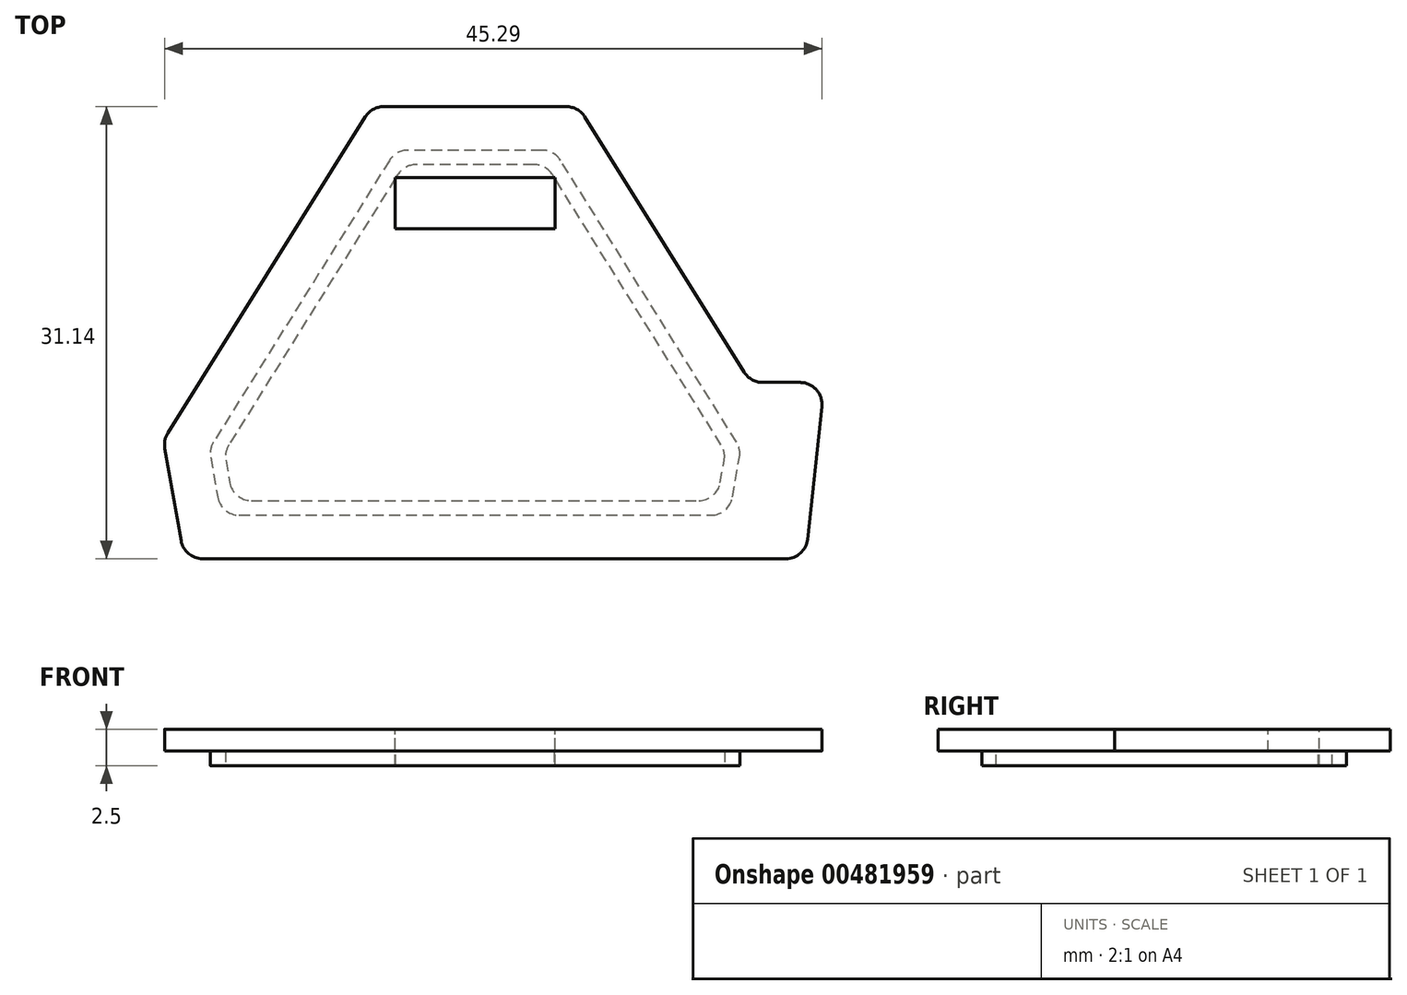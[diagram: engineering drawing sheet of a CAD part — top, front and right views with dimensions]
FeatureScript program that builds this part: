
annotation { "Feature Type Name" : "Feature", "Feature Type Description" : "" }
export const myFeature = defineFeature(function(context is Context, id is Id, definition is map)
    precondition{}
    {
        {
            var Q0;
            Q0=qCreatedBy(makeId("Top.planeOp"),FACE);
            var sketch = newSketch(context, id + "F0", { "sketchPlane" : qUnion([Q0])});
            skLineSegment(sketch, "E0.0", {"start": v(-7.77, 38.07) * mm, "end": v(6.47, 38.07) * mm});
            skLineSegment(sketch, "E1.0", {"start": v(6.47, 38.07) * mm, "end": v(20.82, 15.1) * mm});
            skLineSegment(sketch, "E2.0", {"start": v(19.38, 6.93) * mm, "end": v(20.82, 15.1) * mm});
            skLineSegment(sketch, "E3.0", {"start": v(-20.68, 6.93) * mm, "end": v(19.38, 6.93) * mm});
            skLineSegment(sketch, "E4.0", {"start": v(-20.68, 6.93) * mm, "end": v(-22.12, 15.1) * mm});
            skLineSegment(sketch, "E5.0", {"start": v(-22.12, 15.1) * mm, "end": v(-7.77, 38.07) * mm});
            skSolve(sketch);
        }
        {
            var Q0;
            Q0 = qSketchRegion(id + "F0", true);
            extrude(context, id + "F1", {"entities" : qUnion([Q0]), "depth" : 1.5 * mm});
        }
        {
            var Q0;
            Q0=makeQuery(id+"F1.opExtrude","CAP_FACE",FACE,{"disambiguationData":[OSD([sQuery(id+"F0.wireOp",EDGE,"E0.0"),sQuery(id+"F0.wireOp",EDGE,"E1.0"),sQuery(id+"F0.wireOp",EDGE,"E2.0"),sQuery(id+"F0.wireOp",EDGE,"E3.0"),sQuery(id+"F0.wireOp",EDGE,"E4.0"),sQuery(id+"F0.wireOp",EDGE,"E5.0")])],"isStart":true});
            var sketch = newSketch(context, id + "F2", { "sketchPlane" : qUnion([Q0])});
            skLineSegment(sketch, "E6.0", {"start": v(-18.97, -14.48) * mm, "end": v(-18.16, -9.93) * mm});
            skLineSegment(sketch, "E6.1", {"start": v(16.86, -9.93) * mm, "end": v(17.67, -14.48) * mm});
            skLineSegment(sketch, "E6.2", {"start": v(17.67, -14.48) * mm, "end": v(4.8, -35.07) * mm});
            skLineSegment(sketch, "E6.3", {"start": v(-18.16, -9.93) * mm, "end": v(16.86, -9.93) * mm});
            skLineSegment(sketch, "E6.4", {"start": v(4.8, -35.07) * mm, "end": v(-6.1, -35.07) * mm});
            skLineSegment(sketch, "E6.5", {"start": v(-6.1, -35.07) * mm, "end": v(-18.97, -14.48) * mm});
            skLineSegment(sketch, "E7.1", {"start": v(-5.55, -34.07) * mm, "end": v(-17.91, -14.28) * mm});
            skLineSegment(sketch, "E7.2", {"start": v(4.25, -34.07) * mm, "end": v(-5.55, -34.07) * mm});
            skLineSegment(sketch, "E7.3", {"start": v(16.61, -14.28) * mm, "end": v(4.25, -34.07) * mm});
            skLineSegment(sketch, "E8.0", {"start": v(-17.91, -14.28) * mm, "end": v(-17.32, -10.93) * mm});
            skLineSegment(sketch, "E9.0", {"start": v(16.02, -10.93) * mm, "end": v(16.61, -14.28) * mm});
            skLineSegment(sketch, "E10.trimOffspring", {"start": v(-17.32, -10.93) * mm, "end": v(16.02, -10.93) * mm});
            skSolve(sketch);
        }
        {
            var Q0;
            Q0 = qSketchRegion(id + "F2", true);
            extrude(context, id + "F3", {"entities" : qUnion([Q0]), "operationType" : NewBodyOperationType.ADD, "depth" : 1 * mm});
        }
        {
            var Q0;
            {var subQ0=sQuery(id+"F0.wireOp",EDGE,"E2.0");var subQ1=sQuery(id+"F0.wireOp",EDGE,"E5.0");var subQ2=sQuery(id+"F0.wireOp",EDGE,"E4.0");var subQ3=sQuery(id+"F0.wireOp",EDGE,"E0.0");var subQ4=sQuery(id+"F0.wireOp",EDGE,"E3.0");var subQ5=sQuery(id+"F0.wireOp",EDGE,"E1.0");Q0=makeQuery(id+"F3.boolean.opBoolean","SPLIT",FACE,{"disambiguationData":[TD([makeQuery(id+"F1.opExtrude","SWEPT_FACE",FACE,{"disambiguationData":[OSD([subQ3])]})])],"derivedFrom":makeQuery(id+"F1.opExtrude","CAP_FACE",FACE,{"disambiguationData":[OSD([subQ3,subQ5,subQ0,subQ4,subQ2,subQ1])],"isStart":true})});}
            var sketch = newSketch(context, id + "F4", { "sketchPlane" : qUnion([Q0])});
            skLineSegment(sketch, "E11", {"start": v(16.86, -9.93) * mm, "end": v(16.86, -6.93) * mm});
            skLineSegment(sketch, "E12", {"start": v(16.86, -6.93) * mm, "end": v(22.11, -6.93) * mm});
            skLineSegment(sketch, "E13", {"start": v(22.11, -6.93) * mm, "end": v(23.42, -19.07) * mm});
            skLineSegment(sketch, "E14", {"start": v(23.42, -19.07) * mm, "end": v(16.59, -19.07) * mm});
            skLineSegment(sketch, "E15", {"start": v(16.59, -19.07) * mm, "end": v(16.86, -9.93) * mm});
            skSolve(sketch);
        }
        {
            var Q0;
            Q0 = qSketchRegion(id + "F4", true);
            extrude(context, id + "F5", {"entities" : qUnion([Q0]), "operationType" : NewBodyOperationType.ADD, "oppositeDirection" : true, "depth" : 1.5 * mm});
        }
        {
            var Q0;
            Q0=makeQuery(id+"F5.opExtrude","SWEPT_EDGE",EDGE,{"disambiguationData":[OSD([sQuery(id+"F4.wireOp",EDGE,"E13"),sQuery(id+"F4.wireOp",EDGE,"E14")])]});
            var Q1;
            Q1=makeQuery(id+"F5.boolean.opBoolean","INTERSECT",EDGE,{"derivedFrom":[makeQuery(id+"F1.opExtrude","SWEPT_FACE",FACE,{"disambiguationData":[OSD([sQuery(id+"F0.wireOp",EDGE,"E1.0")])]}),makeQuery(id+"F5.opExtrude","SWEPT_FACE",FACE,{"disambiguationData":[OSD([sQuery(id+"F4.wireOp",EDGE,"E14")])]})]});
            var Q2;
            Q2=makeQuery(id+"F5.opExtrude","SWEPT_EDGE",EDGE,{"disambiguationData":[OSD([sQuery(id+"F4.wireOp",EDGE,"E12"),sQuery(id+"F4.wireOp",EDGE,"E13")])]});
            var Q3;
            Q3=makeQuery(id+"F1.opExtrude","SWEPT_EDGE",EDGE,{"disambiguationData":[OSD([sQuery(id+"F0.wireOp",EDGE,"E3.0"),sQuery(id+"F0.wireOp",EDGE,"E4.0")])]});
            var Q4;
            Q4=makeQuery(id+"F1.opExtrude","SWEPT_EDGE",EDGE,{"disambiguationData":[OSD([sQuery(id+"F0.wireOp",EDGE,"E4.0"),sQuery(id+"F0.wireOp",EDGE,"E5.0")])]});
            var Q5;
            Q5=makeQuery(id+"F1.opExtrude","SWEPT_EDGE",EDGE,{"disambiguationData":[OSD([sQuery(id+"F0.wireOp",EDGE,"E0.0"),sQuery(id+"F0.wireOp",EDGE,"E5.0")])]});
            var Q6;
            Q6=makeQuery(id+"F1.opExtrude","SWEPT_EDGE",EDGE,{"disambiguationData":[OSD([sQuery(id+"F0.wireOp",EDGE,"E0.0"),sQuery(id+"F0.wireOp",EDGE,"E1.0")])]});
            var Q7;
            Q7=makeQuery(id+"F3.opExtrude","SWEPT_EDGE",EDGE,{"disambiguationData":[OSD([sQuery(id+"F2.wireOp",EDGE,"E6.2"),sQuery(id+"F2.wireOp",EDGE,"E6.4")])]});
            var Q8;
            Q8=makeQuery(id+"F3.opExtrude","SWEPT_EDGE",EDGE,{"disambiguationData":[OSD([sQuery(id+"F2.wireOp",EDGE,"E6.4"),sQuery(id+"F2.wireOp",EDGE,"E6.5")])]});
            var Q9;
            Q9=makeQuery(id+"F3.opExtrude","SWEPT_EDGE",EDGE,{"disambiguationData":[OSD([sQuery(id+"F2.wireOp",EDGE,"E6.0"),sQuery(id+"F2.wireOp",EDGE,"E6.5")])]});
            var Q10;
            Q10=makeQuery(id+"F3.opExtrude","SWEPT_EDGE",EDGE,{"disambiguationData":[OSD([sQuery(id+"F2.wireOp",EDGE,"E6.0"),sQuery(id+"F2.wireOp",EDGE,"E6.3")])]});
            var Q11;
            Q11=makeQuery(id+"F3.opExtrude","SWEPT_EDGE",EDGE,{"disambiguationData":[OSD([sQuery(id+"F2.wireOp",EDGE,"E6.1"),sQuery(id+"F2.wireOp",EDGE,"E6.3")])]});
            var Q12;
            Q12=makeQuery(id+"F3.opExtrude","SWEPT_EDGE",EDGE,{"disambiguationData":[OSD([sQuery(id+"F2.wireOp",EDGE,"E6.1"),sQuery(id+"F2.wireOp",EDGE,"E6.2")])]});
            var Q13;
            Q13=makeQuery(id+"F3.opExtrude","SWEPT_EDGE",EDGE,{"disambiguationData":[OSD([sQuery(id+"F2.wireOp",EDGE,"E8.0"),sQuery(id+"F2.wireOp",EDGE,"E10.trimOffspring")])]});
            var Q14;
            Q14=makeQuery(id+"F3.opExtrude","SWEPT_EDGE",EDGE,{"disambiguationData":[OSD([sQuery(id+"F2.wireOp",EDGE,"E7.1"),sQuery(id+"F2.wireOp",EDGE,"E8.0")])]});
            var Q15;
            Q15=makeQuery(id+"F3.opExtrude","SWEPT_EDGE",EDGE,{"disambiguationData":[OSD([sQuery(id+"F2.wireOp",EDGE,"E7.1"),sQuery(id+"F2.wireOp",EDGE,"E7.2")])]});
            var Q16;
            Q16=makeQuery(id+"F3.opExtrude","SWEPT_EDGE",EDGE,{"disambiguationData":[OSD([sQuery(id+"F2.wireOp",EDGE,"E7.2"),sQuery(id+"F2.wireOp",EDGE,"E7.3")])]});
            var Q17;
            Q17=makeQuery(id+"F3.opExtrude","SWEPT_EDGE",EDGE,{"disambiguationData":[OSD([sQuery(id+"F2.wireOp",EDGE,"E9.0"),sQuery(id+"F2.wireOp",EDGE,"E10.trimOffspring")])]});
            var Q18;
            Q18=makeQuery(id+"F3.opExtrude","SWEPT_EDGE",EDGE,{"disambiguationData":[OSD([sQuery(id+"F2.wireOp",EDGE,"E7.3"),sQuery(id+"F2.wireOp",EDGE,"E9.0")])]});
            fillet(context, id + "F6", {"entities" : qUnion([Q0, Q1, Q2, Q3, Q4, Q5, Q6, Q7, Q8, Q9, Q10, Q11, Q12, Q13, Q14, Q15, Q16, Q17, Q18]), "radius" : 1.5 * mm, "tangentPropagation" : true, "allowEdgeOverflow" : false});
        }
        {
            var Q0;
            Q0=makeQuery(id+"F5.boolean.opBoolean","MERGE",FACE,{"derivedFrom":[makeQuery(id+"F1.opExtrude","CAP_FACE",FACE,{"disambiguationData":[OSD([sQuery(id+"F0.wireOp",EDGE,"E0.0"),sQuery(id+"F0.wireOp",EDGE,"E1.0"),sQuery(id+"F0.wireOp",EDGE,"E2.0"),sQuery(id+"F0.wireOp",EDGE,"E3.0"),sQuery(id+"F0.wireOp",EDGE,"E4.0"),sQuery(id+"F0.wireOp",EDGE,"E5.0")])],"isStart":false}),makeQuery(id+"F5.opExtrude","CAP_FACE",FACE,{"disambiguationData":[OSD([sQuery(id+"F4.wireOp",EDGE,"E11"),sQuery(id+"F4.wireOp",EDGE,"E12"),sQuery(id+"F4.wireOp",EDGE,"E13"),sQuery(id+"F4.wireOp",EDGE,"E14"),sQuery(id+"F4.wireOp",EDGE,"E15")])],"isStart":false})]});
            var sketch = newSketch(context, id + "F7", { "sketchPlane" : qUnion([Q0])});
            skLineSegment(sketch, "E16", {"start": v(-6.94, 38.07) * mm, "end": v(5.64, 38.07) * mm});
            skLineSegment(sketch, "E17.0", {"start": v(-6.15, 33.17) * mm, "end": v(4.85, 33.17) * mm});
            skLineSegment(sketch, "E18.0", {"start": v(-6.15, 29.67) * mm, "end": v(4.85, 29.67) * mm});
            skLineSegment(sketch, "E19.0", {"start": v(-6.15, 33.17) * mm, "end": v(-6.15, 29.67) * mm});
            skLineSegment(sketch, "E20.0", {"start": v(4.85, 33.17) * mm, "end": v(4.85, 29.67) * mm});
            skPoint(sketch, "E21.end.orphan", {"position": v(-0.65, 29.67) * mm});
            skPoint(sketch, "E21.start.orphan", {"position": v(-0.65, 33.17) * mm});
            skPoint(sketch, "E22.orphan", {"position": v(-6.94, 33.17) * mm});
            skPoint(sketch, "E23.orphan", {"position": v(-6.94, 29.67) * mm});
            skPoint(sketch, "E24.orphan", {"position": v(5.64, 33.17) * mm});
            skPoint(sketch, "E25.orphan", {"position": v(5.64, 29.67) * mm});
            skSolve(sketch);
        }
        {
            var Q0;
            Q0 = qSketchRegion(id + "F7", true);
            extrude(context, id + "F8", {"entities" : qUnion([Q0]), "operationType" : NewBodyOperationType.REMOVE, "oppositeDirection" : true, "depth" : 25 * mm});
        }
    });
